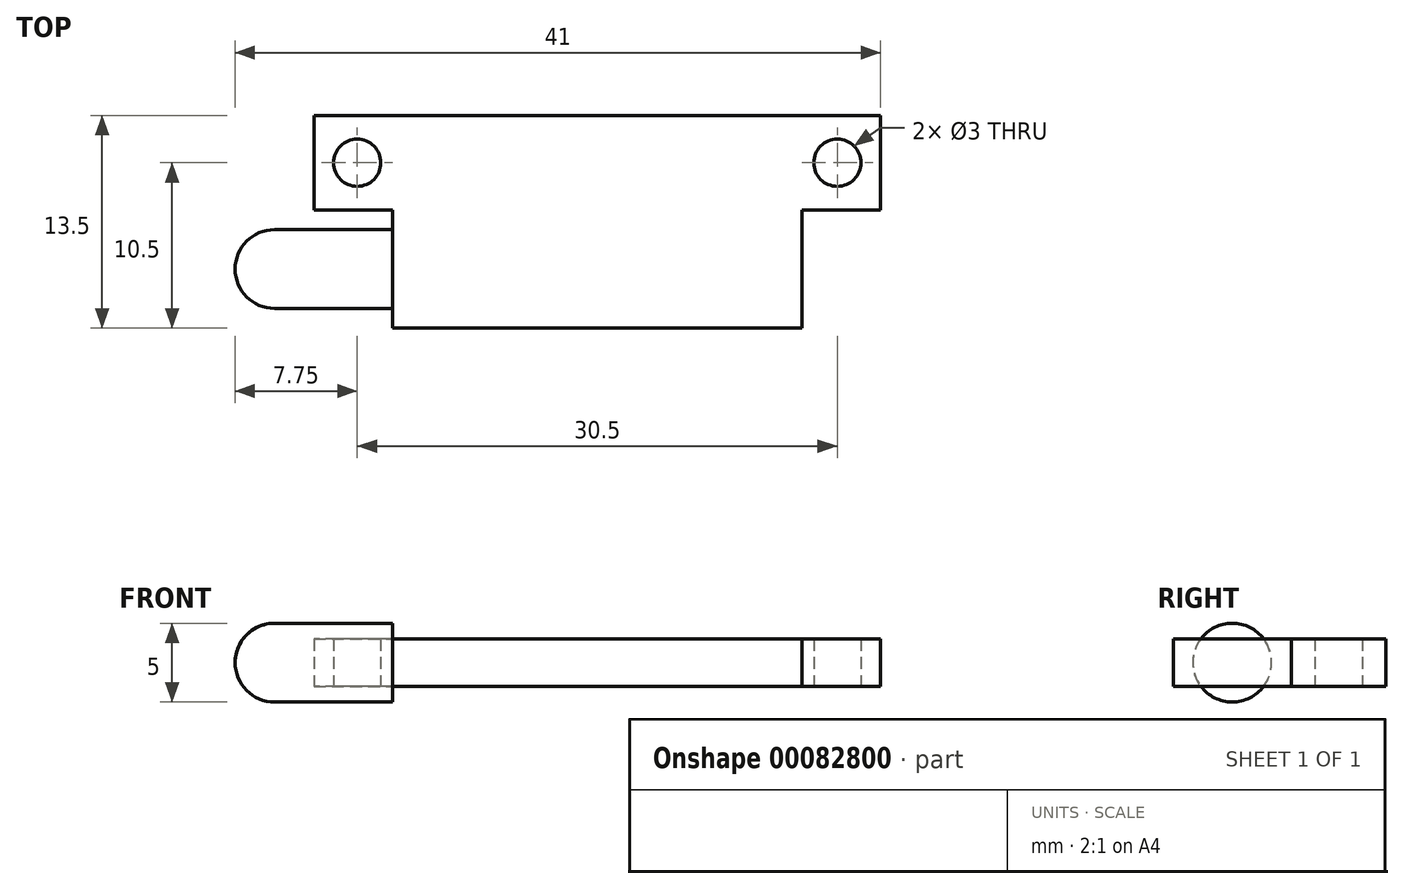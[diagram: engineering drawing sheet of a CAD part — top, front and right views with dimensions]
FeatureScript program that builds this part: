
annotation { "Feature Type Name" : "Feature", "Feature Type Description" : "" }
export const myFeature = defineFeature(function(context is Context, id is Id, definition is map)
    precondition{}
    {
        {
            var Q0;
            Q0=qCreatedBy(makeId("Top.planeOp"),FACE);
            var sketch = newSketch(context, id + "F0", { "sketchPlane" : qUnion([Q0])});
            skLineSegment(sketch, "E0.bottom", {"start": v(18, 6.75) * mm, "end": v(-18, 6.75) * mm});
            skLineSegment(sketch, "E0.top", {"start": v(18, -6.75) * mm, "end": v(-18, -6.75) * mm});
            skLineSegment(sketch, "E0.left", {"start": v(18, 6.75) * mm, "end": v(18, -6.75) * mm});
            skLineSegment(sketch, "E0.right", {"start": v(-18, 6.75) * mm, "end": v(-18, -6.75) * mm});
            skPoint(sketch, "E0.middle", {"position": v(0, 0) * mm});
            skCircle(sketch, "E1", {"center": v(-15.25, 3.75) * mm, "radius": 1.5 * mm});
            skCircle(sketch, "E2.MirrorC", {"center": v(15.25, 3.75) * mm, "radius": 1.5 * mm});
            skLineSegment(sketch, "E3.bottom", {"start": v(-18, -6.75) * mm, "end": v(-13, -6.75) * mm});
            skLineSegment(sketch, "E3.top", {"start": v(-18, 0.75) * mm, "end": v(-13, 0.75) * mm});
            skLineSegment(sketch, "E3.left", {"start": v(-18, -6.75) * mm, "end": v(-18, 0.75) * mm});
            skLineSegment(sketch, "E3.right", {"start": v(-13, -6.75) * mm, "end": v(-13, 0.75) * mm});
            skLineSegment(sketch, "E4.MirrorCS", {"start": v(18, 0.75) * mm, "end": v(13, 0.75) * mm});
            skLineSegment(sketch, "E5.MirrorCS", {"start": v(13, -6.75) * mm, "end": v(13, 0.75) * mm});
            skSolve(sketch);
        }
        {
            var Q0;
            {var subQ2=sQuery(id+"F0.wireOp",EDGE,"E0.bottom");Q0=makeQuery(id+"F0.imprint","IMPRINT",FACE,{"disambiguationData":[TD([[makeQuery(id+"F0.imprint","IMPRINT",EDGE,{"derivedFrom":subQ2}),1.0]])]});}
            extrude(context, id + "F1", {"entities" : qUnion([Q0]), "depth" : 3 * mm});
        }
        {
            var Q0;
            Q0=makeQuery(id+"F1.opExtrude","SWEPT_FACE",FACE,{"disambiguationData":[OSD([sQuery(id+"F0.wireOp",EDGE,"E3.right")])]});
            var sketch = newSketch(context, id + "F2", { "sketchPlane" : qUnion([Q0])});
            skLineSegment(sketch, "E6.0.0", {"start": v(-0.75, 0) * mm, "end": v(6.75, 0) * mm, "construction": true});
            skLineSegment(sketch, "E6.0.1", {"start": v(6.75, 0) * mm, "end": v(6.75, 3) * mm, "construction": true});
            skLineSegment(sketch, "E6.0.2", {"start": v(6.75, 3) * mm, "end": v(-0.75, 3) * mm, "construction": true});
            skLineSegment(sketch, "E6.0.3", {"start": v(-0.75, 3) * mm, "end": v(-0.75, 0) * mm, "construction": true});
            skCircle(sketch, "E7", {"center": v(3, 1.5) * mm, "radius": 2.5 * mm});
            skPoint(sketch, "E7.centerSnap0", {"position": v(-0.75, 1.5) * mm});
            skPoint(sketch, "E7.centerSnap1", {"position": v(3, 3) * mm});
            skSolve(sketch);
        }
        {
            var Q0;
            {var subQ0=sQuery(id+"F2.wireOp",EDGE,"E7");var subQ1=makeQuery(id+"F1.opExtrude","CAP_EDGE",EDGE,{"disambiguationData":[OSD([sQuery(id+"F0.wireOp",EDGE,"E3.right")])],"isStart":true});var subQ2=makeQuery(id+"F2.imprint","INTERSECT",VERTEX,{"disambiguationData":[OD(0.0)],"derivedFrom":[subQ1,subQ0]});Q0=makeQuery(id+"F2.imprint","IMPRINT",FACE,{"disambiguationData":[TD([[makeQuery(id+"F2.imprint","IMPRINT",EDGE,{"disambiguationData":[TD([[subQ2,-1.0]])],"derivedFrom":subQ0}),1.0]])]});}
            var Q1;
            {var subQ0=sQuery(id+"F2.wireOp",EDGE,"E7");var subQ1=sQuery(id+"F0.wireOp",EDGE,"E3.right");var subQ2=makeQuery(id+"F1.opExtrude","CAP_EDGE",EDGE,{"disambiguationData":[OSD([subQ1])],"isStart":false});var subQ3=makeQuery(id+"F2.imprint","INTERSECT",VERTEX,{"disambiguationData":[OD(0.0)],"derivedFrom":[subQ2,subQ0]});Q1=makeQuery(id+"F2.imprint","IMPRINT",FACE,{"disambiguationData":[TD([[makeQuery(id+"F2.imprint","IMPRINT",EDGE,{"disambiguationData":[TD([[subQ3,-1.0]])],"derivedFrom":subQ0}),1.0]])]});}
            var Q2;
            {var subQ0=sQuery(id+"F2.wireOp",EDGE,"E7");var subQ1=makeQuery(id+"F1.opExtrude","CAP_EDGE",EDGE,{"disambiguationData":[OSD([sQuery(id+"F0.wireOp",EDGE,"E3.right")])],"isStart":false});var subQ2=makeQuery(id+"F2.imprint","INTERSECT",VERTEX,{"disambiguationData":[OD(0.0)],"derivedFrom":[subQ1,subQ0]});Q2=makeQuery(id+"F2.imprint","IMPRINT",FACE,{"disambiguationData":[TD([[makeQuery(id+"F2.imprint","IMPRINT",EDGE,{"disambiguationData":[TD([[subQ2,1.0]])],"derivedFrom":subQ0}),1.0]])]});}
            extrude(context, id + "F3", {"entities" : qUnion([Q0, Q1, Q2]), "operationType" : NewBodyOperationType.ADD, "depth" : 10 * mm});
        }
        {
            var Q0;
            Q0=makeQuery(id+"F4VUVvN7flEydy9_1.1.F3.opExtrude","CAP_EDGE",EDGE,{"disambiguationData":[OSD([sQuery(id+"F2.wireOp",EDGE,"E7")])],"isStart":false});
            var Q1;
            Q1=makeQuery(id+"F3.opExtrude","CAP_EDGE",EDGE,{"disambiguationData":[OSD([sQuery(id+"F2.wireOp",EDGE,"E7")])],"isStart":false});
            fillet(context, id + "F4", {"entities" : qUnion([Q0, Q1]), "radius" : 2.5 * mm, "tangentPropagation" : true, "allowEdgeOverflow" : false});
        }
    });
